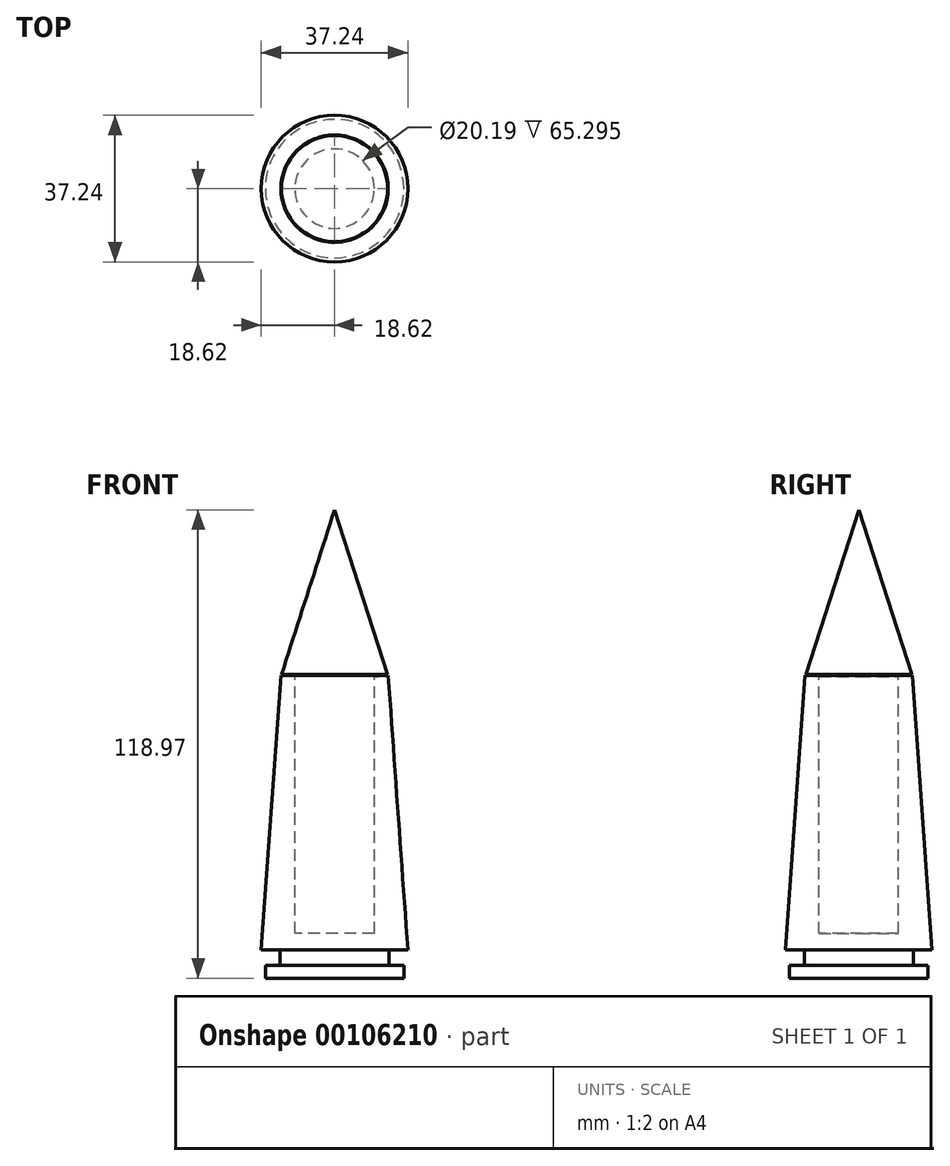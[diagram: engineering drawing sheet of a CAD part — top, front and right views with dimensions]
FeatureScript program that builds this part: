
annotation { "Feature Type Name" : "Feature", "Feature Type Description" : "" }
export const myFeature = defineFeature(function(context is Context, id is Id, definition is map)
    precondition{}
    {
        {
            var Q0;
            Q0=qCreatedBy(makeId("Front.planeOp"),FACE);
            var sketch = newSketch(context, id + "F0", { "sketchPlane" : qUnion([Q0])});
            skLineSegment(sketch, "E0", {"start": v(0, 0) * mm, "end": v(-17.58, 0) * mm});
            skLineSegment(sketch, "E1", {"start": v(-17.58, 0) * mm, "end": v(-17.58, 3.23) * mm});
            skLineSegment(sketch, "E2", {"start": v(-17.58, 3.23) * mm, "end": v(-13.84, 3.23) * mm});
            skLineSegment(sketch, "E3", {"start": v(-13.84, 3.23) * mm, "end": v(-13.84, 7.18) * mm});
            skLineSegment(sketch, "E4", {"start": v(-13.84, 7.18) * mm, "end": v(-18.62, 7.18) * mm});
            skLineSegment(sketch, "E5", {"start": v(-18.62, 7.18) * mm, "end": v(-13.63, 76.89) * mm});
            skLineSegment(sketch, "E6", {"start": v(-13.63, 76.89) * mm, "end": v(-10.1, 76.64) * mm});
            skLineSegment(sketch, "E7", {"start": v(-10.1, 76.64) * mm, "end": v(-10.1, 11.34) * mm});
            skLineSegment(sketch, "E8", {"start": v(-10.1, 11.34) * mm, "end": v(0, 11.34) * mm});
            skLineSegment(sketch, "E9", {"start": v(0, 11.34) * mm, "end": v(0, 0) * mm});
            skSolve(sketch);
        }
        {
            var Q0;
            Q0=makeQuery(id+"F0.imprint","IMPRINT",FACE,{"disambiguationData":[TD([[makeQuery(id+"F0.imprint","IMPRINT",EDGE,{"derivedFrom":sQuery(id+"F0.wireOp",EDGE,"E0")}),-1.0]])]});
            var Q1;
            Q1=sQuery(id+"F0.wireOp",EDGE,"E9");
            revolve(context, id + "F1", {"entities" : qUnion([Q0]), "axis" : qUnion([Q1]), "revolveType" : RevolveType.FULL});
        }
        {
            var Q0;
            Q0=qCreatedBy(makeId("Front.planeOp"),FACE);
            var sketch = newSketch(context, id + "F2", { "sketchPlane" : qUnion([Q0])});
            skLineSegment(sketch, "E10", {"start": v(-13.48, 77.16) * mm, "end": v(0, 118.97) * mm});
            skLineSegment(sketch, "E11", {"start": v(0, 118.97) * mm, "end": v(0, 77.16) * mm});
            skLineSegment(sketch, "E12", {"start": v(0, 77.16) * mm, "end": v(-13.48, 77.16) * mm});
            skSolve(sketch);
        }
        {
            var Q0;
            Q0=makeQuery(id+"F2.imprint","IMPRINT",FACE,{"disambiguationData":[TD([[makeQuery(id+"F2.imprint","IMPRINT",EDGE,{"derivedFrom":sQuery(id+"F2.wireOp",EDGE,"E10")}),-1.0]])]});
            var Q1;
            Q1=sQuery(id+"F2.wireOp",EDGE,"E11");
            revolve(context, id + "F3", {"entities" : qUnion([Q0]), "axis" : qUnion([Q1]), "revolveType" : RevolveType.FULL});
        }
    });
